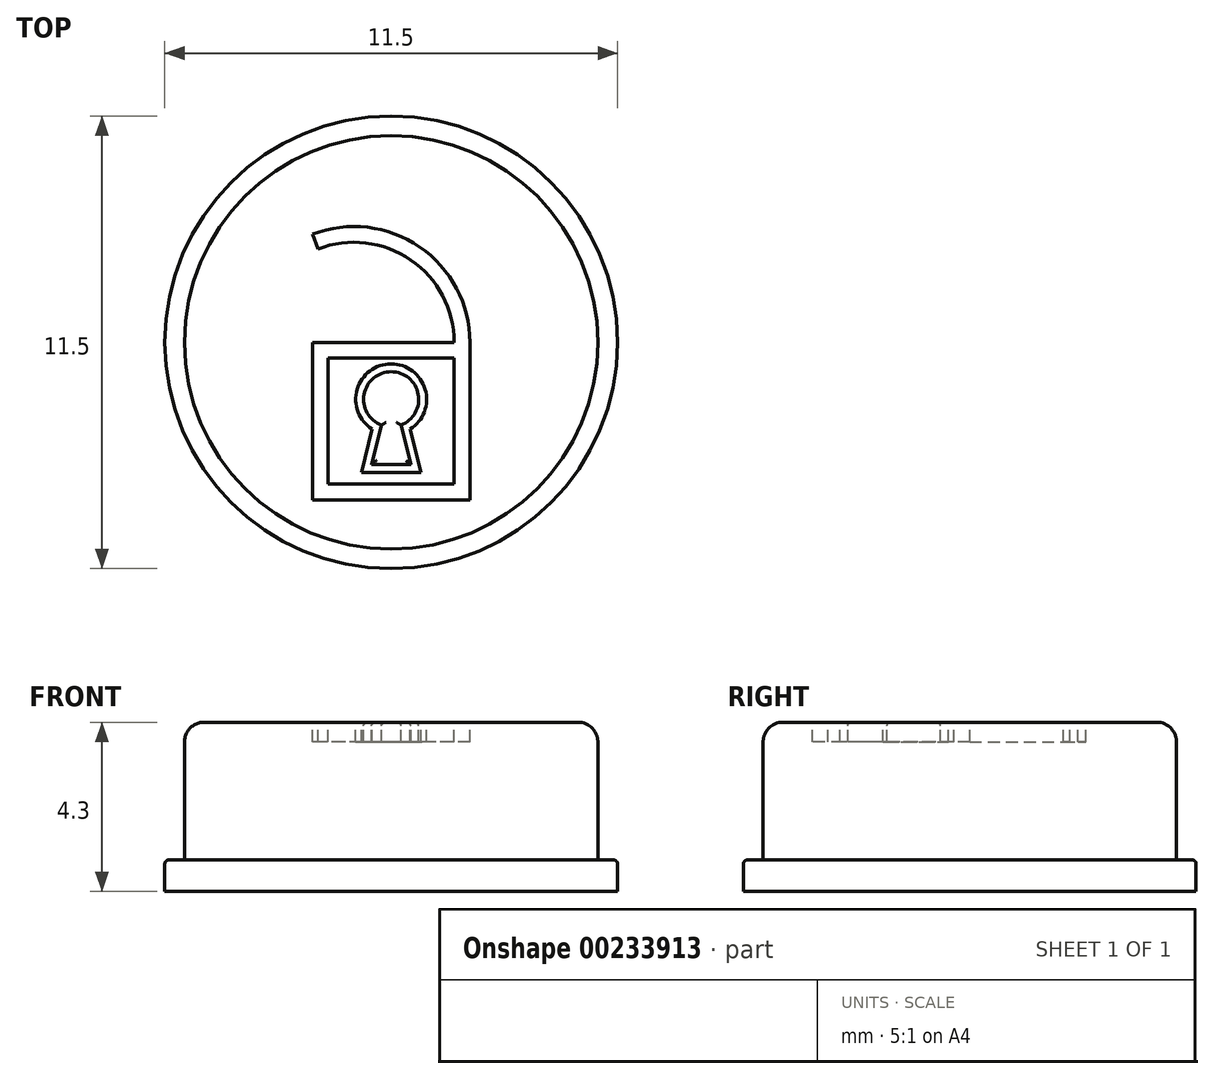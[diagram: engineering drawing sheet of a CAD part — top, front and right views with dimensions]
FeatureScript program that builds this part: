
annotation { "Feature Type Name" : "Feature", "Feature Type Description" : "" }
export const myFeature = defineFeature(function(context is Context, id is Id, definition is map)
    precondition{}
    {
        {
            var Q0;
            Q0=qCreatedBy(makeId("Front.planeOp"),FACE);
            var sketch = newSketch(context, id + "F0", { "sketchPlane" : qUnion([Q0])});
            skLineSegment(sketch, "E0.bottom", {"start": v(0, 0) * mm, "end": v(-5.75, 0) * mm});
            skLineSegment(sketch, "E0.top", {"start": v(-5.25, 0.8) * mm, "end": v(-5.75, 0.8) * mm});
            skLineSegment(sketch, "E0.left", {"start": v(0, 0) * mm, "end": v(0, 0.8) * mm});
            skLineSegment(sketch, "E0.right", {"start": v(-5.75, 0) * mm, "end": v(-5.75, 0.8) * mm});
            skLineSegment(sketch, "E1.top", {"start": v(0, 4.3) * mm, "end": v(-5.25, 4.3) * mm});
            skLineSegment(sketch, "E1.left", {"start": v(0, 0.8) * mm, "end": v(0, 4.3) * mm});
            skLineSegment(sketch, "E1.right", {"start": v(-5.25, 0.8) * mm, "end": v(-5.25, 4.3) * mm});
            skSolve(sketch);
        }
        {
            var Q0;
            Q0=makeQuery(id+"F0.imprint","IMPRINT",FACE,{"disambiguationData":[TD([[makeQuery(id+"F0.imprint","IMPRINT",EDGE,{"derivedFrom":sQuery(id+"F0.wireOp",EDGE,"E0.bottom")}),-1.0]])]});
            var Q1;
            Q1=sQuery(id+"F0.wireOp",EDGE,"E1.left");
            revolve(context, id + "F1", {"entities" : qUnion([Q0]), "axis" : qUnion([Q1]), "revolveType" : RevolveType.FULL});
        }
        {
            var Q0;
            Q0=makeQuery(id+"F1.opRevolve","SWEPT_FACE",FACE,{"disambiguationData":[OSD([sQuery(id+"F0.wireOp",EDGE,"E1.top")])]});
            var sketch = newSketch(context, id + "F2", { "sketchPlane" : qUnion([Q0])});
            skLineSegment(sketch, "E2.bottom", {"start": v(1.6, 0) * mm, "end": v(-2, 0) * mm});
            skLineSegment(sketch, "E2.top", {"start": v(2, -4) * mm, "end": v(-2, -4) * mm});
            skLineSegment(sketch, "E2.left", {"start": v(2, 0) * mm, "end": v(2, -4) * mm});
            skLineSegment(sketch, "E2.right", {"start": v(-2, 0) * mm, "end": v(-2, -4) * mm});
            skArc(sketch, "E3", {"start": v(2, 0) * mm, "mid": v(0.72, 2.43) * mm, "end": v(-2, 2.75) * mm});
            skArc(sketch, "E4.0", {"start": v(1.6, 0) * mm, "mid": v(0.5, 2.1) * mm, "end": v(-1.86, 2.37) * mm});
            skLineSegment(sketch, "E5", {"start": v(-1.86, 2.37) * mm, "end": v(-2, 2.75) * mm});
            skLineSegment(sketch, "E6.0", {"start": v(1.6, -0.4) * mm, "end": v(-1.6, -0.4) * mm});
            skLineSegment(sketch, "E6.1", {"start": v(1.6, -0.4) * mm, "end": v(1.6, -3.6) * mm});
            skLineSegment(sketch, "E6.2", {"start": v(1.6, -3.6) * mm, "end": v(-1.6, -3.6) * mm});
            skLineSegment(sketch, "E6.3", {"start": v(-1.6, -0.4) * mm, "end": v(-1.6, -3.6) * mm});
            skLineSegment(sketch, "E7.top", {"start": v(-0.5, -3.1) * mm, "end": v(0.5, -3.1) * mm});
            skLineSegment(sketch, "E8", {"start": v(-0.25, -2.1) * mm, "end": v(-0.5, -3.1) * mm});
            skLineSegment(sketch, "E9", {"start": v(0.25, -2.1) * mm, "end": v(0.5, -3.1) * mm});
            skArc(sketch, "E10", {"start": v(0.25, -2.1) * mm, "mid": v(0, -0.75) * mm, "end": v(-0.25, -2.1) * mm});
            skArc(sketch, "E11.0", {"start": v(0.48, -2.2) * mm, "mid": v(0, -0.55) * mm, "end": v(-0.48, -2.2) * mm});
            skLineSegment(sketch, "E11.1", {"start": v(0.48, -2.2) * mm, "end": v(0.76, -3.3) * mm});
            skLineSegment(sketch, "E11.2", {"start": v(-0.76, -3.3) * mm, "end": v(0.76, -3.3) * mm});
            skLineSegment(sketch, "E11.3", {"start": v(-0.48, -2.2) * mm, "end": v(-0.76, -3.3) * mm});
            skSolve(sketch);
        }
        {
            var Q0;
            Q0=makeQuery(id+"F2.imprint","IMPRINT",FACE,{"disambiguationData":[TD([[makeQuery(id+"F2.imprint","IMPRINT",EDGE,{"derivedFrom":sQuery(id+"F2.wireOp",EDGE,"E2.bottom")}),1.0]])]});
            var Q1;
            Q1=makeQuery(id+"F2.imprint","IMPRINT",FACE,{"disambiguationData":[TD([[makeQuery(id+"F2.imprint","IMPRINT",EDGE,{"derivedFrom":sQuery(id+"F2.wireOp",EDGE,"E7.top")}),-1.0]])]});
            extrude(context, id + "F3", {"entities" : qUnion([Q0, Q1]), "operationType" : NewBodyOperationType.REMOVE, "oppositeDirection" : true, "depth" : 0.5 * mm});
        }
        {
            var Q0;
            Q0=makeQuery(id+"F1.opRevolve","SWEPT_EDGE",EDGE,{"disambiguationData":[OSD([sQuery(id+"F0.wireOp",EDGE,"E1.top"),sQuery(id+"F0.wireOp",EDGE,"E1.right")])]});
            fillet(context, id + "F4", {"entities" : qUnion([Q0]), "radius" : 0.5 * mm, "tangentPropagation" : true, "allowEdgeOverflow" : false});
        }
        {
            var Q0;
            Q0=makeQuery(id+"F3.boolean.opBoolean","COPY",EDGE,{"derivedFrom":makeQuery(id+"F3.opExtrude","CAP_EDGE",EDGE,{"disambiguationData":[OSD([sQuery(id+"F2.wireOp",EDGE,"E11.0")])],"isStart":true})});
            var Q1;
            Q1=makeQuery(id+"F3.boolean.opBoolean","COPY",EDGE,{"derivedFrom":makeQuery(id+"F3.opExtrude","CAP_EDGE",EDGE,{"disambiguationData":[OSD([sQuery(id+"F2.wireOp",EDGE,"E11.2")])],"isStart":true})});
            var Q2;
            Q2=makeQuery(id+"F3.boolean.opBoolean","COPY",EDGE,{"derivedFrom":makeQuery(id+"F3.opExtrude","CAP_EDGE",EDGE,{"disambiguationData":[OSD([sQuery(id+"F2.wireOp",EDGE,"E11.1")])],"isStart":true})});
            var Q3;
            Q3=makeQuery(id+"F3.boolean.opBoolean","COPY",EDGE,{"derivedFrom":makeQuery(id+"F3.opExtrude","CAP_EDGE",EDGE,{"disambiguationData":[OSD([sQuery(id+"F2.wireOp",EDGE,"E11.3")])],"isStart":true})});
            var Q4;
            Q4=makeQuery(id+"F3.boolean.opBoolean","SPLIT",FACE,{"disambiguationData":[TD([makeQuery(id+"F3.opExtrude","SWEPT_FACE",FACE,{"disambiguationData":[OSD([sQuery(id+"F2.wireOp",EDGE,"E7.top")])]})])],"derivedFrom":makeQuery(id+"F1.opRevolve","SWEPT_FACE",FACE,{"disambiguationData":[OSD([sQuery(id+"F0.wireOp",EDGE,"E1.top")])]})});
            var Q5;
            Q5=makeQuery(id+"F3.boolean.opBoolean","COPY",EDGE,{"derivedFrom":makeQuery(id+"F3.opExtrude","CAP_EDGE",EDGE,{"disambiguationData":[OSD([sQuery(id+"F2.wireOp",EDGE,"E4.0")])],"isStart":true})});
            var Q6;
            Q6=makeQuery(id+"F3.boolean.opBoolean","COPY",EDGE,{"derivedFrom":makeQuery(id+"F3.opExtrude","CAP_EDGE",EDGE,{"disambiguationData":[OSD([sQuery(id+"F2.wireOp",EDGE,"E2.bottom")])],"isStart":true})});
            var Q7;
            Q7=makeQuery(id+"F3.boolean.opBoolean","COPY",EDGE,{"derivedFrom":makeQuery(id+"F3.opExtrude","CAP_EDGE",EDGE,{"disambiguationData":[OSD([sQuery(id+"F2.wireOp",EDGE,"E2.left")])],"isStart":true})});
            var Q8;
            Q8=makeQuery(id+"F3.boolean.opBoolean","COPY",EDGE,{"derivedFrom":makeQuery(id+"F3.opExtrude","CAP_EDGE",EDGE,{"disambiguationData":[OSD([sQuery(id+"F2.wireOp",EDGE,"E2.top")])],"isStart":true})});
            var Q9;
            Q9=makeQuery(id+"F3.boolean.opBoolean","COPY",EDGE,{"derivedFrom":makeQuery(id+"F3.opExtrude","CAP_EDGE",EDGE,{"disambiguationData":[OSD([sQuery(id+"F2.wireOp",EDGE,"E2.right")])],"isStart":true})});
            var Q10;
            Q10=makeQuery(id+"F3.boolean.opBoolean","COPY",EDGE,{"derivedFrom":makeQuery(id+"F3.opExtrude","CAP_EDGE",EDGE,{"disambiguationData":[OSD([sQuery(id+"F2.wireOp",EDGE,"E5")])],"isStart":true})});
            var Q11;
            Q11=makeQuery(id+"F3.boolean.opBoolean","COPY",EDGE,{"derivedFrom":makeQuery(id+"F3.opExtrude","CAP_EDGE",EDGE,{"disambiguationData":[OSD([sQuery(id+"F2.wireOp",EDGE,"E6.0")])],"isStart":true})});
            var Q12;
            Q12=makeQuery(id+"F3.boolean.opBoolean","COPY",EDGE,{"derivedFrom":makeQuery(id+"F3.opExtrude","CAP_EDGE",EDGE,{"disambiguationData":[OSD([sQuery(id+"F2.wireOp",EDGE,"E6.1")])],"isStart":true})});
            var Q13;
            Q13=makeQuery(id+"F3.boolean.opBoolean","COPY",EDGE,{"derivedFrom":makeQuery(id+"F3.opExtrude","CAP_EDGE",EDGE,{"disambiguationData":[OSD([sQuery(id+"F2.wireOp",EDGE,"E6.2")])],"isStart":true})});
            var Q14;
            Q14=makeQuery(id+"F3.boolean.opBoolean","COPY",EDGE,{"derivedFrom":makeQuery(id+"F3.opExtrude","CAP_EDGE",EDGE,{"disambiguationData":[OSD([sQuery(id+"F2.wireOp",EDGE,"E6.3")])],"isStart":true})});
            var Q15;
            Q15=makeQuery(id+"F1.opRevolve","SWEPT_EDGE",EDGE,{"disambiguationData":[OSD([sQuery(id+"F0.wireOp",EDGE,"E0.top"),sQuery(id+"F0.wireOp",EDGE,"E0.right")])]});
            fillet(context, id + "F5", {"entities" : qUnion([Q0, Q1, Q2, Q3, Q4, Q5, Q6, Q7, Q8, Q9, Q10, Q11, Q12, Q13, Q14, Q15]), "radius" : 0.1 * mm, "tangentPropagation" : true, "allowEdgeOverflow" : false});
        }
    });
